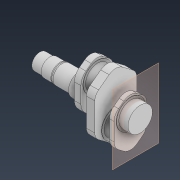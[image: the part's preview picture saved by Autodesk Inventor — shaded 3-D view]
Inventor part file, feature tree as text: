
AUTODESK INVENTOR PART (.ipt)
format: ipt  version: 2022 (Build 260153000, 153)  size: 297,472 bytes
history: native  units: mm
features: sketch x11, extrude x11, plane x3, revolve x1, projected_geometry x1
ambient origin geometry x8: Origin, YZ Plane, XZ Plane, XY Plane, X Axis, Y Axis, Z Axis, Center Point
bodies: Solid1 (feature_tree)
feature tree (27):
  revolve  "Revolution1"  [1 undecoded]
  plane  "Work Plane7"
  sketch  "Sketch22"  dims[d3=44.0mm d4=36.0mm]
  extrude  "Extrusion18"  Depth=44.0mm
  extrude  "Extrusion19"  Depth=42.0mm
  extrude  "Extrusion20"  Depth=25.5mm
  extrude  "Extrusion21"  TaperAngle=90.0deg  [1 undecoded]
  plane  "Work Plane8"
  extrude  "Extrusion22"  Depth=50.0mm
  extrude  "Extrusion23"  Depth=14.76mm
  extrude  "Extrusion24"  Depth=55.0mm
  extrude  "Extrusion25"  Depth=22.0mm TaperAngle=0.0deg
  extrude  "Extrusion26"  Depth=1.0mm
  extrude  "Extrusion27"  Depth=21.0mm
  extrude  "Extrusion28"  Depth=21.0mm
  plane  "Work Plane9"
  sketch  "Sketch1"  dims[d1=23.0mm d2=23.0mm]
  sketch  "Sketch23"  dims[d6=40.0mm d7=42.0mm]
  sketch  "Sketch24"  dims[d9=25.5mm d10=2.0mm]
  sketch  "Sketch25"  dims[d11=1.5mm d12=90.0deg]
  sketch  "Sketch26"  dims[d13=65.0mm d14=50.0mm]
  sketch  "Sketch27"  dims[d15=1.0mm d96=14.76mm]
  sketch  "Sketch28"  dims[d97=65.0mm d98=55.0mm]
  sketch  "Sketch29"  dims[d99=34.5mm d100=22.0mm d101=0.0mm]
  sketch  "Sketch30"  dims[d102=1.0mm d103=0.0mm d105=15.0mm]
  projected_geometry  "Projected Loop9"
  sketch  "Sketch31"  dims[d106=74.0mm d107=27.2mm d108=51.2mm d109=2.0mm d110=10.0mm d111=0.0mm d112=1.0mm d113=0.0mm d114=18.91mm d115=65.0mm d116=69.0mm d117=1.0mm d118=0.0mm d119=25.0mm d120=29.9mm d122=95.0mm d124=1.0mm d125=0.0mm d126=2.0mm d127=2.0mm d128=55.0mm d129=21.0mm d130=0.0mm d131=1.0mm d132=0.0mm d133=15.0mm d134=25.0mm d135=40.4mm d136=25.0mm d137=10.43mm d138=0.0mm d139=65.0mm d140=1.0mm d141=0.0mm d142=55.0mm d143=21.0mm d144=0.0mm d41=0.5mm d42=0.872665mm d43=0.5mm d44=0.872665mm d91=0.5mm d92=0.872665mm d93=0.5mm d94=0.872665mm]
note: 2 required parameter values undecoded (feature->parameter linkage not recoverable at this tier; creation-order binding heuristic only, values carry confidence <= 0.55)